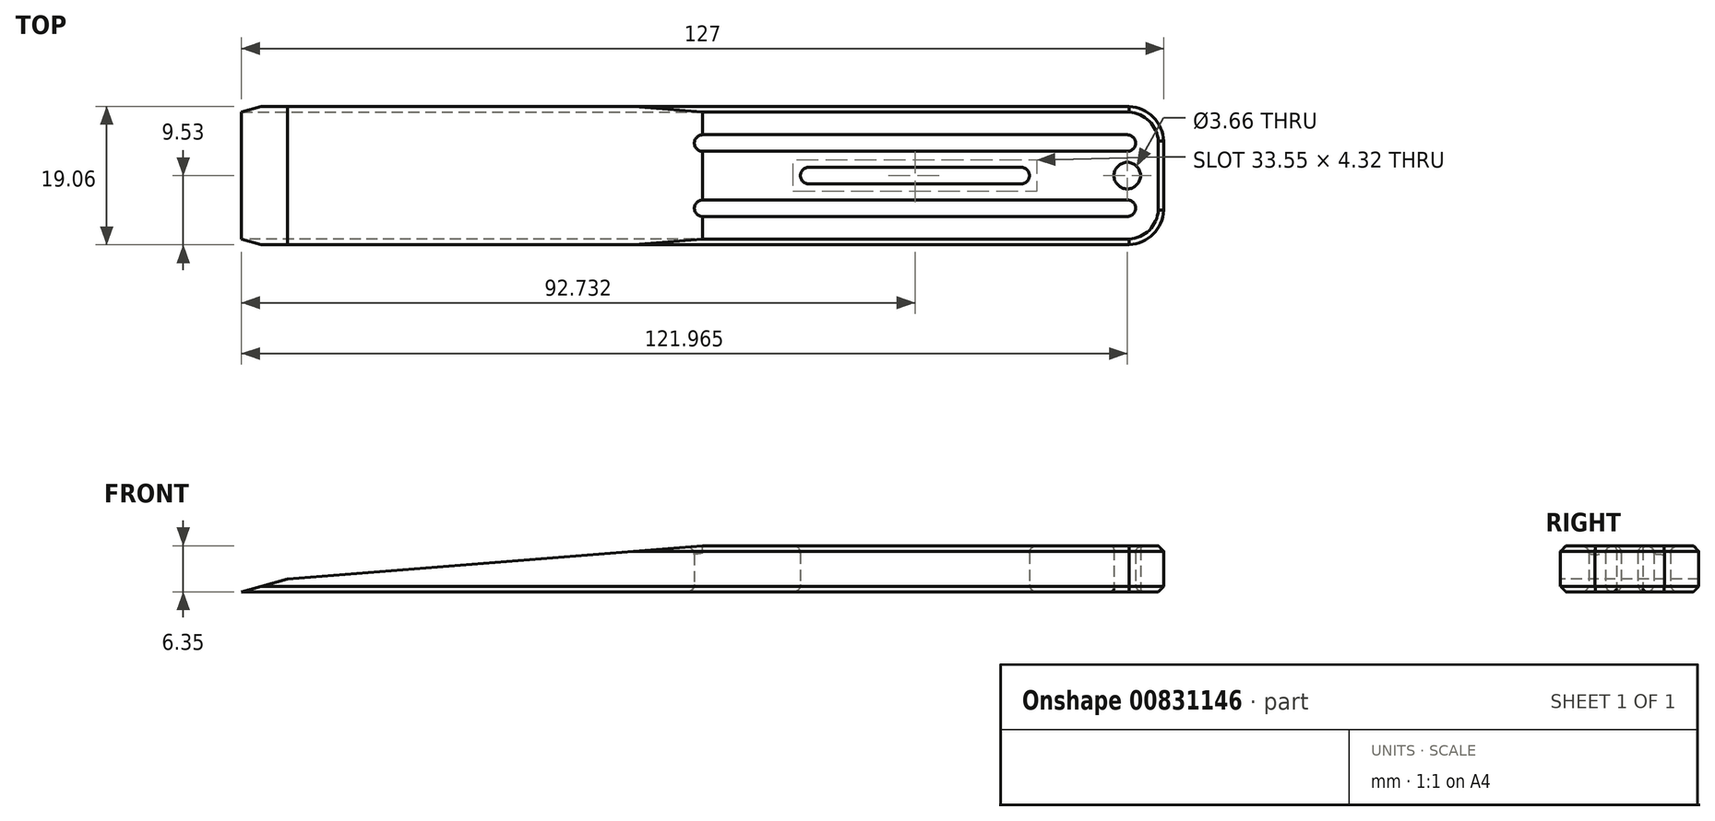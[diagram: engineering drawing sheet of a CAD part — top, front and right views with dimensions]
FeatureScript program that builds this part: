
annotation { "Feature Type Name" : "Feature", "Feature Type Description" : "" }
export const myFeature = defineFeature(function(context is Context, id is Id, definition is map)
    precondition{}
    {
        {
            var Q0;
            Q0=qCreatedBy(makeId("Top.planeOp"),FACE);
            var sketch = newSketch(context, id + "F0", { "sketchPlane" : qUnion([Q0])});
            skLineSegment(sketch, "E0.left", {"start": v(-63.5, 9.53) * mm, "end": v(-63.5, -9.53) * mm});
            skPoint(sketch, "E0.middle", {"position": v(0, 0) * mm});
            skArc(sketch, "E1", {"start": v(63.5, 4.77) * mm, "mid": v(62.03, 8.06) * mm, "end": v(58.73, 9.53) * mm});
            skArc(sketch, "E2.MirrorCS", {"start": v(63.5, -4.77) * mm, "mid": v(62.03, -8.06) * mm, "end": v(58.73, -9.53) * mm});
            skLineSegment(sketch, "E3", {"start": v(58.46, 4.49) * mm, "end": v(0, 4.49) * mm});
            skLineSegment(sketch, "E4", {"start": v(58.46, -4.49) * mm, "end": v(0, -4.49) * mm});
            skPoint(sketch, "E5.startSnap0", {"position": v(29.23, -4.49) * mm});
            skLineSegment(sketch, "E6", {"start": v(14.62, 0) * mm, "end": v(43.85, 0) * mm});
            skArc(sketch, "E7.0.startCap", {"start": v(58.46, 5.63) * mm, "mid": v(59.6, 4.49) * mm, "end": v(58.46, 3.35) * mm});
            skArc(sketch, "E7.0.endCap", {"start": v(0, 3.35) * mm, "mid": v(-1.14, 4.49) * mm, "end": v(0, 5.63) * mm});
            skLineSegment(sketch, "E7.0.left", {"start": v(58.46, 3.35) * mm, "end": v(0, 3.35) * mm});
            skLineSegment(sketch, "E7.0.right", {"start": v(58.46, 5.63) * mm, "end": v(0, 5.63) * mm});
            skArc(sketch, "E8.0.startCap", {"start": v(14.62, -1.14) * mm, "mid": v(13.47, 0) * mm, "end": v(14.62, 1.14) * mm});
            skArc(sketch, "E8.0.endCap", {"start": v(43.85, 1.14) * mm, "mid": v(45, 0) * mm, "end": v(43.85, -1.14) * mm});
            skLineSegment(sketch, "E8.0.left", {"start": v(14.62, 1.14) * mm, "end": v(43.85, 1.14) * mm});
            skLineSegment(sketch, "E8.0.right", {"start": v(14.62, -1.14) * mm, "end": v(43.85, -1.14) * mm});
            skArc(sketch, "E8.1.startCap", {"start": v(58.46, -3.35) * mm, "mid": v(59.6, -4.49) * mm, "end": v(58.46, -5.63) * mm});
            skArc(sketch, "E8.1.endCap", {"start": v(0, -5.63) * mm, "mid": v(-1.14, -4.49) * mm, "end": v(0, -3.35) * mm});
            skLineSegment(sketch, "E8.1.left", {"start": v(58.46, -5.63) * mm, "end": v(0, -5.63) * mm});
            skLineSegment(sketch, "E8.1.right", {"start": v(58.46, -3.35) * mm, "end": v(0, -3.35) * mm});
            skLineSegment(sketch, "E9", {"start": v(-63.5, -9.53) * mm, "end": v(58.73, -9.53) * mm});
            skLineSegment(sketch, "E10", {"start": v(-63.5, 9.53) * mm, "end": v(58.73, 9.53) * mm});
            skLineSegment(sketch, "E11", {"start": v(63.5, 4.77) * mm, "end": v(63.5, -4.77) * mm});
            skCircle(sketch, "E12", {"center": v(58.46, 0) * mm, "radius": 1.83 * mm});
            skSolve(sketch);
        }
        {
            var Q0;
            Q0=makeQuery(id+"F0.imprint","IMPRINT",FACE,{"disambiguationData":[TD([[makeQuery(id+"F0.imprint","IMPRINT",EDGE,{"derivedFrom":sQuery(id+"F0.wireOp",EDGE,"E0.left")}),1.0]])]});
            extrude(context, id + "F1", {"entities" : qUnion([Q0]), "depth" : 6.35 * mm, "offsetDistance" : 25.4 * mm});
        }
        {
            var Q0;
            Q0=makeQuery(id+"F1.opExtrude","CAP_EDGE",EDGE,{"disambiguationData":[OSD([sQuery(id+"F0.wireOp",EDGE,"E0.left")])],"isStart":false});
            chamfer(context, id + "F2", {"entities" : qUnion([Q0]), "chamferType" : ChamferType.TWO_OFFSETS, "width1" : 63.5 * mm, "oppositeDirection" : false, "width2" : 5.08 * mm, "tangentPropagation" : true});
        }
        {
            var Q0;
            {var subQ0=sQuery(id+"F0.wireOp",EDGE,"E0.left");Q0=makeQuery(id+"F2.opChamfer","BLEND_EDGE",EDGE,{"blendedFrom":[makeQuery(id+"F1.opExtrude","CAP_EDGE",EDGE,{"disambiguationData":[OSD([subQ0])],"isStart":false}),makeQuery(id+"F1.opExtrude","SWEPT_FACE",FACE,{"disambiguationData":[OSD([subQ0])]})],"blendedInto":[makeQuery(id+"F1.opExtrude","SWEPT_FACE",FACE,{"disambiguationData":[OSD([subQ0])]})]});}
            chamfer(context, id + "F3", {"entities" : qUnion([Q0]), "chamferType" : ChamferType.TWO_OFFSETS, "width1" : 1.27 * mm, "oppositeDirection" : false, "width2" : 6.35 * mm, "tangentPropagation" : true});
        }
        {
            var Q0;
            Q0=makeQuery(id+"F1.opExtrude","CAP_EDGE",EDGE,{"disambiguationData":[OSD([sQuery(id+"F0.wireOp",EDGE,"E8.1.right")])],"isStart":false});
            var Q1;
            Q1=makeQuery(id+"F2.opChamfer","BLEND_EDGE",EDGE,{"blendedFrom":[makeQuery(id+"F1.opExtrude","CAP_EDGE",EDGE,{"disambiguationData":[OSD([sQuery(id+"F0.wireOp",EDGE,"E0.left")])],"isStart":false}),makeQuery(id+"F1.opExtrude","SWEPT_FACE",FACE,{"disambiguationData":[OSD([sQuery(id+"F0.wireOp",EDGE,"E8.1.endCap")])]})],"blendedInto":[makeQuery(id+"F1.opExtrude","SWEPT_FACE",FACE,{"disambiguationData":[OSD([sQuery(id+"F0.wireOp",EDGE,"E8.1.endCap")])]})]});
            var Q2;
            Q2=makeQuery(id+"F2.opChamfer","BLEND_EDGE",EDGE,{"blendedFrom":[makeQuery(id+"F1.opExtrude","CAP_EDGE",EDGE,{"disambiguationData":[OSD([sQuery(id+"F0.wireOp",EDGE,"E0.left")])],"isStart":false}),makeQuery(id+"F1.opExtrude","SWEPT_FACE",FACE,{"disambiguationData":[OSD([sQuery(id+"F0.wireOp",EDGE,"E7.0.endCap")])]})],"blendedInto":[makeQuery(id+"F1.opExtrude","SWEPT_FACE",FACE,{"disambiguationData":[OSD([sQuery(id+"F0.wireOp",EDGE,"E7.0.endCap")])]})]});
            var Q3;
            Q3=makeQuery(id+"F1.opExtrude","CAP_EDGE",EDGE,{"disambiguationData":[OSD([sQuery(id+"F0.wireOp",EDGE,"E7.0.right")])],"isStart":false});
            var Q4;
            Q4=makeQuery(id+"F1.opExtrude","CAP_EDGE",EDGE,{"disambiguationData":[OSD([sQuery(id+"F0.wireOp",EDGE,"E7.0.left")])],"isStart":false});
            var Q5;
            Q5=makeQuery(id+"F1.opExtrude","CAP_EDGE",EDGE,{"disambiguationData":[OSD([sQuery(id+"F0.wireOp",EDGE,"E8.1.left")])],"isStart":false});
            var Q6;
            Q6=makeQuery(id+"F1.opExtrude","CAP_EDGE",EDGE,{"disambiguationData":[OSD([sQuery(id+"F0.wireOp",EDGE,"E8.1.startCap")])],"isStart":false});
            var Q7;
            Q7=makeQuery(id+"F1.opExtrude","CAP_EDGE",EDGE,{"disambiguationData":[OSD([sQuery(id+"F0.wireOp",EDGE,"E7.0.startCap")])],"isStart":false});
            var Q8;
            Q8=makeQuery(id+"F1.opExtrude","CAP_EDGE",EDGE,{"disambiguationData":[OSD([sQuery(id+"F0.wireOp",EDGE,"E8.0.endCap")])],"isStart":false});
            var Q9;
            Q9=makeQuery(id+"F1.opExtrude","CAP_EDGE",EDGE,{"disambiguationData":[OSD([sQuery(id+"F0.wireOp",EDGE,"E8.0.right")])],"isStart":false});
            var Q10;
            Q10=makeQuery(id+"F1.opExtrude","CAP_EDGE",EDGE,{"disambiguationData":[OSD([sQuery(id+"F0.wireOp",EDGE,"E8.0.left")])],"isStart":false});
            var Q11;
            Q11=makeQuery(id+"F1.opExtrude","CAP_EDGE",EDGE,{"disambiguationData":[OSD([sQuery(id+"F0.wireOp",EDGE,"E8.0.startCap")])],"isStart":false});
            var Q12;
            Q12=makeQuery(id+"F1.opExtrude","CAP_EDGE",EDGE,{"disambiguationData":[OSD([sQuery(id+"F0.wireOp",EDGE,"E8.1.left")])],"isStart":true});
            var Q13;
            Q13=makeQuery(id+"F1.opExtrude","CAP_EDGE",EDGE,{"disambiguationData":[OSD([sQuery(id+"F0.wireOp",EDGE,"E8.1.right")])],"isStart":true});
            var Q14;
            Q14=makeQuery(id+"F1.opExtrude","CAP_EDGE",EDGE,{"disambiguationData":[OSD([sQuery(id+"F0.wireOp",EDGE,"E8.1.endCap")])],"isStart":true});
            var Q15;
            Q15=makeQuery(id+"F1.opExtrude","CAP_EDGE",EDGE,{"disambiguationData":[OSD([sQuery(id+"F0.wireOp",EDGE,"E8.1.startCap")])],"isStart":true});
            var Q16;
            Q16=makeQuery(id+"F1.opExtrude","CAP_EDGE",EDGE,{"disambiguationData":[OSD([sQuery(id+"F0.wireOp",EDGE,"E8.0.endCap")])],"isStart":true});
            var Q17;
            Q17=makeQuery(id+"F1.opExtrude","CAP_EDGE",EDGE,{"disambiguationData":[OSD([sQuery(id+"F0.wireOp",EDGE,"E8.0.right")])],"isStart":true});
            var Q18;
            Q18=makeQuery(id+"F1.opExtrude","CAP_EDGE",EDGE,{"disambiguationData":[OSD([sQuery(id+"F0.wireOp",EDGE,"E8.0.left")])],"isStart":true});
            var Q19;
            Q19=makeQuery(id+"F1.opExtrude","CAP_EDGE",EDGE,{"disambiguationData":[OSD([sQuery(id+"F0.wireOp",EDGE,"E8.0.startCap")])],"isStart":true});
            var Q20;
            Q20=makeQuery(id+"F1.opExtrude","CAP_EDGE",EDGE,{"disambiguationData":[OSD([sQuery(id+"F0.wireOp",EDGE,"E7.0.right")])],"isStart":true});
            var Q21;
            Q21=makeQuery(id+"F1.opExtrude","CAP_EDGE",EDGE,{"disambiguationData":[OSD([sQuery(id+"F0.wireOp",EDGE,"E7.0.left")])],"isStart":true});
            var Q22;
            Q22=makeQuery(id+"F1.opExtrude","CAP_EDGE",EDGE,{"disambiguationData":[OSD([sQuery(id+"F0.wireOp",EDGE,"E7.0.endCap")])],"isStart":true});
            var Q23;
            Q23=makeQuery(id+"F1.opExtrude","CAP_EDGE",EDGE,{"disambiguationData":[OSD([sQuery(id+"F0.wireOp",EDGE,"E7.0.startCap")])],"isStart":true});
            fillet(context, id + "F4", {"entities" : qUnion([Q0, Q1, Q2, Q3, Q4, Q5, Q6, Q7, Q8, Q9, Q10, Q11, Q12, Q13, Q14, Q15, Q16, Q17, Q18, Q19, Q20, Q21, Q22, Q23]), "radius" : 1.02 * mm, "tangentPropagation" : true, "allowEdgeOverflow" : false});
        }
        {
            var Q0;
            Q0=makeQuery(id+"F1.opExtrude","CAP_EDGE",EDGE,{"disambiguationData":[OSD([sQuery(id+"F0.wireOp",EDGE,"E12")])],"isStart":true});
            var Q1;
            Q1=makeQuery(id+"F1.opExtrude","CAP_EDGE",EDGE,{"disambiguationData":[OSD([sQuery(id+"F0.wireOp",EDGE,"E12")])],"isStart":false});
            fillet(context, id + "F5", {"entities" : qUnion([Q0, Q1]), "radius" : 0.46 * mm, "tangentPropagation" : true, "allowEdgeOverflow" : false});
        }
        {
            var Q0;
            Q0=makeQuery(id+"F1.opExtrude","CAP_EDGE",EDGE,{"disambiguationData":[OSD([sQuery(id+"F0.wireOp",EDGE,"E9")])],"isStart":false});
            var Q1;
            Q1=makeQuery(id+"F1.opExtrude","CAP_EDGE",EDGE,{"disambiguationData":[OSD([sQuery(id+"F0.wireOp",EDGE,"E10")])],"isStart":false});
            var Q2;
            Q2=makeQuery(id+"F1.opExtrude","CAP_EDGE",EDGE,{"disambiguationData":[OSD([sQuery(id+"F0.wireOp",EDGE,"E1")])],"isStart":false});
            var Q3;
            Q3=makeQuery(id+"F1.opExtrude","CAP_EDGE",EDGE,{"disambiguationData":[OSD([sQuery(id+"F0.wireOp",EDGE,"E11")])],"isStart":false});
            var Q4;
            Q4=makeQuery(id+"F1.opExtrude","CAP_EDGE",EDGE,{"disambiguationData":[OSD([sQuery(id+"F0.wireOp",EDGE,"E2.MirrorCS")])],"isStart":false});
            var Q5;
            Q5=makeQuery(id+"F1.opExtrude","CAP_EDGE",EDGE,{"disambiguationData":[OSD([sQuery(id+"F0.wireOp",EDGE,"E1")])],"isStart":true});
            var Q6;
            Q6=makeQuery(id+"F1.opExtrude","CAP_EDGE",EDGE,{"disambiguationData":[OSD([sQuery(id+"F0.wireOp",EDGE,"E11")])],"isStart":true});
            var Q7;
            Q7=makeQuery(id+"F1.opExtrude","CAP_EDGE",EDGE,{"disambiguationData":[OSD([sQuery(id+"F0.wireOp",EDGE,"E2.MirrorCS")])],"isStart":true});
            var Q8;
            Q8=makeQuery(id+"F1.opExtrude","CAP_EDGE",EDGE,{"disambiguationData":[OSD([sQuery(id+"F0.wireOp",EDGE,"E10")])],"isStart":true});
            var Q9;
            Q9=makeQuery(id+"F1.opExtrude","CAP_EDGE",EDGE,{"disambiguationData":[OSD([sQuery(id+"F0.wireOp",EDGE,"E9")])],"isStart":true});
            chamfer(context, id + "F6", {"entities" : qUnion([Q0, Q1, Q2, Q3, Q4, Q5, Q6, Q7, Q8, Q9]), "width" : 0.76 * mm, "tangentPropagation" : true});
        }
    });
